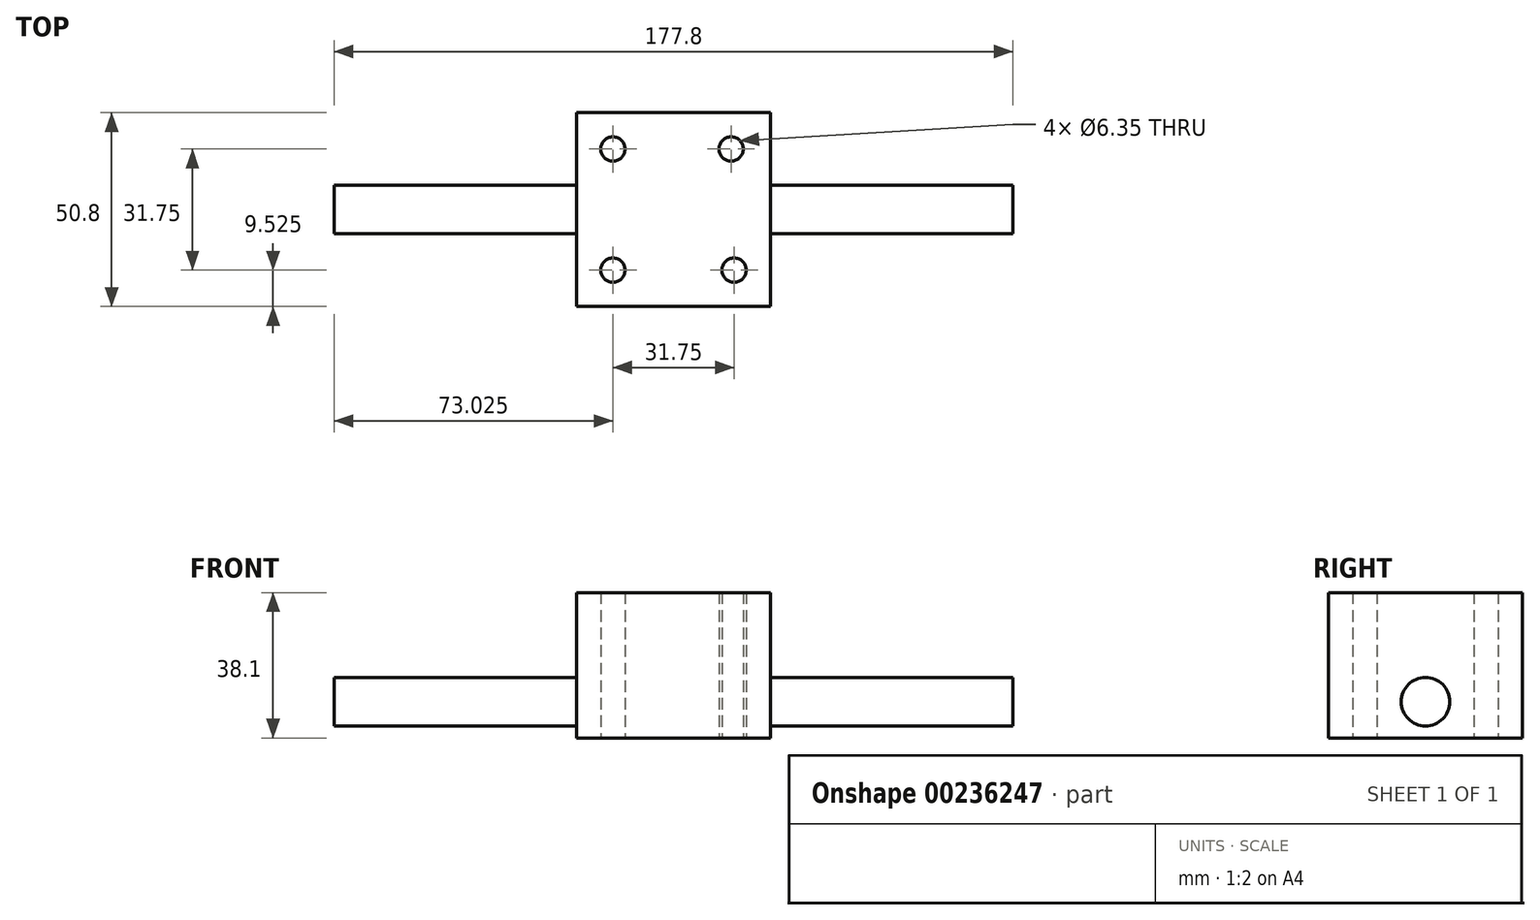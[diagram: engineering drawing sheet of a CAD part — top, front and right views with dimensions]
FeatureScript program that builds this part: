
annotation { "Feature Type Name" : "Feature", "Feature Type Description" : "" }
export const myFeature = defineFeature(function(context is Context, id is Id, definition is map)
    precondition{}
    {
        {
            var Q0;
            Q0=qCreatedBy(makeId("Top.planeOp"),FACE);
            var sketch = newSketch(context, id + "F0", { "sketchPlane" : qUnion([Q0])});
            skLineSegment(sketch, "E0.bottom", {"start": v(25.4, 25.4) * mm, "end": v(-25.4, 25.4) * mm});
            skLineSegment(sketch, "E0.top", {"start": v(25.4, -25.4) * mm, "end": v(-25.4, -25.4) * mm});
            skLineSegment(sketch, "E0.left", {"start": v(25.4, 25.4) * mm, "end": v(25.4, -25.4) * mm});
            skLineSegment(sketch, "E0.right", {"start": v(-25.4, 25.4) * mm, "end": v(-25.4, -25.4) * mm});
            skPoint(sketch, "E0.middle", {"position": v(0, 0) * mm});
            skCircle(sketch, "E1", {"center": v(-15.88, 15.88) * mm, "radius": 3.18 * mm});
            skCircle(sketch, "E2", {"center": v(15.1, 15.88) * mm, "radius": 3.18 * mm});
            skCircle(sketch, "E3", {"center": v(-15.88, -15.88) * mm, "radius": 3.18 * mm});
            skCircle(sketch, "E4", {"center": v(15.88, -15.88) * mm, "radius": 3.18 * mm});
            skSolve(sketch);
        }
        {
            var Q0;
            Q0 = qSketchRegion(id + "F0", true);
            extrude(context, id + "F1", {"entities" : qUnion([Q0]), "endBound" : BoundingType.SYMMETRIC, "depth" : 38.1 * mm});
        }
        {
            var Q0;
            Q0=qCreatedBy(makeId("Right.planeOp"),FACE);
            var sketch = newSketch(context, id + "F2", { "sketchPlane" : qUnion([Q0])});
            skCircle(sketch, "E5", {"center": v(0, -9.53) * mm, "radius": 6.35 * mm});
            skSolve(sketch);
        }
        {
            var Q0;
            Q0 = qSketchRegion(id + "F2", true);
            extrude(context, id + "F3", {"entities" : qUnion([Q0]), "operationType" : NewBodyOperationType.ADD, "endBound" : BoundingType.SYMMETRIC, "depth" : 177.8 * mm});
        }
    });
